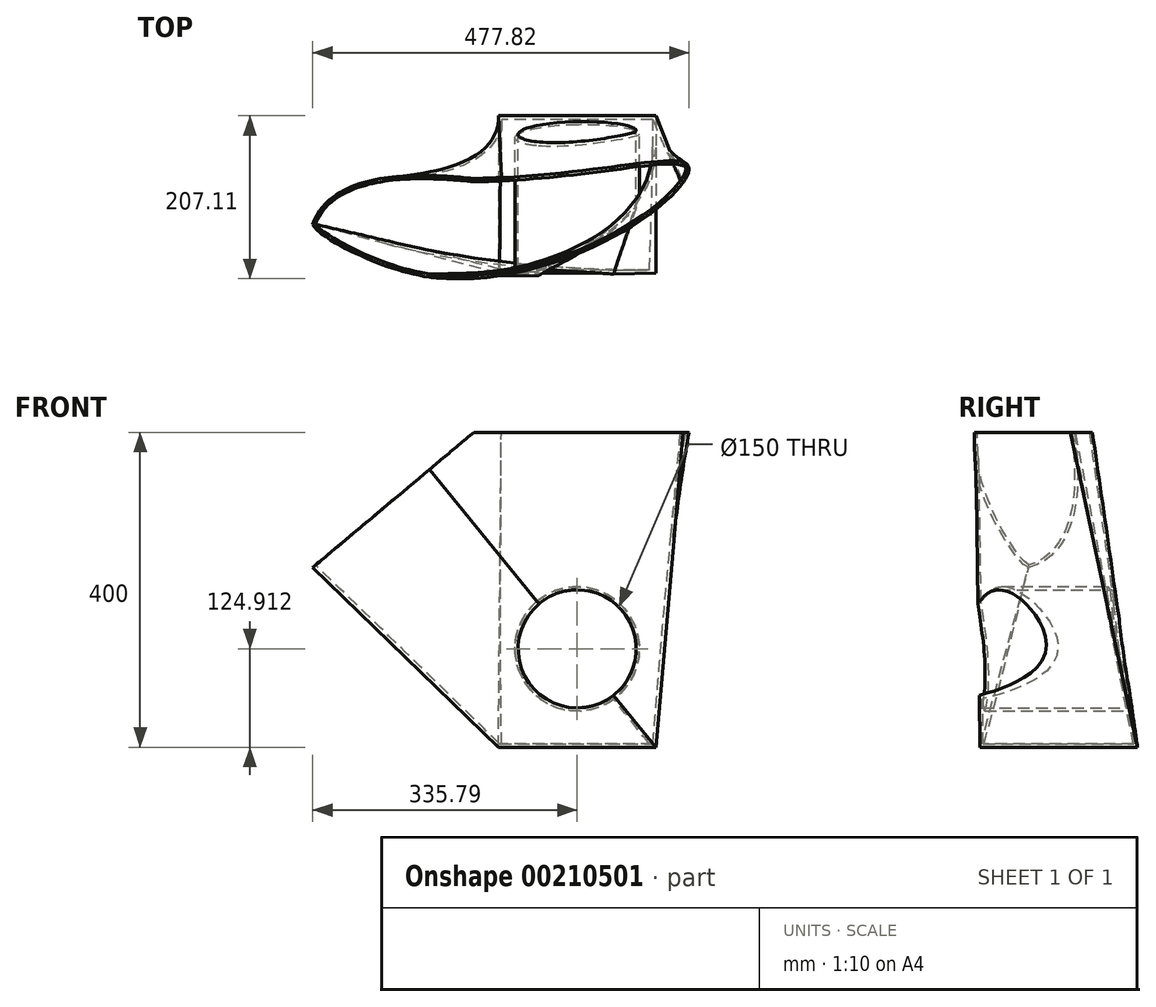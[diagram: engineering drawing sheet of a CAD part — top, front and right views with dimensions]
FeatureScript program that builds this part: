
annotation { "Feature Type Name" : "Feature", "Feature Type Description" : "" }
export const myFeature = defineFeature(function(context is Context, id is Id, definition is map)
    precondition{}
    {
        {
            var Q0;
            Q0=qCreatedBy(makeId("Top.planeOp"),FACE);
            var sketch = newSketch(context, id + "F0", { "sketchPlane" : qUnion([Q0])});
            skLineSegment(sketch, "E0.rect.bottom", {"start": v(-100, 100) * mm, "end": v(100, 100) * mm});
            skLineSegment(sketch, "E0.rect.top", {"start": v(-100, -100) * mm, "end": v(100, -100) * mm});
            skLineSegment(sketch, "E0.rect.left", {"start": v(-100, 100) * mm, "end": v(-100, -100) * mm});
            skLineSegment(sketch, "E0.rect.right", {"start": v(100, 100) * mm, "end": v(100, -100) * mm});
            skPoint(sketch, "E0.rect.middle", {"position": v(0, 0) * mm});
            skSolve(sketch);
        }
        {
            var Q0;
            Q0=qCreatedBy(makeId("Top.planeOp"),FACE);
            cPlane(context, id + "F1", {"entities" : qUnion([Q0]), "cplaneType" : CPlaneType.OFFSET, "offset" : 400 * mm, "width" : 150 * mm, "height" : 150 * mm});
        }
        {
            var Q0;
            Q0=qCreatedBy(id+"F1.planeOp",FACE);
            var sketch = newSketch(context, id + "F2", { "sketchPlane" : qUnion([Q0])});
            skFitSpline(sketch, "E1", {"points": [v(-520.65, 0) * mm, v(-72.7, 22.78) * mm, v(141.98, 33.22) * mm, v(-117.9, -105.72) * mm, v(-520.65, 0) * mm]});
            skSolve(sketch);
        }
        {
            var Q0;
            Q0=makeQuery(id+"F0.imprint","IMPRINT",FACE,{"disambiguationData":[TD([[makeQuery(id+"F0.imprint","IMPRINT",EDGE,{"derivedFrom":sQuery(id+"F0.wireOp",EDGE,"E0.rect.bottom")}),-1.0]])]});
            var Q1;
            Q1=makeQuery(id+"F2.imprint","IMPRINT",FACE,{"disambiguationData":[TD([[makeQuery(id+"F2.imprint","IMPRINT",EDGE,{"derivedFrom":sQuery(id+"F2.wireOp",EDGE,"E1")}),-1.0]])]});
            loft(context, id + "F3", {"sheetProfilesArray" : [{ "sheetProfileEntities" : qUnion([Q0]) }, { "sheetProfileEntities" : qUnion([Q1]) }]});
        }
        {
            var Q0;
            Q0=qCreatedBy(makeId("Front.planeOp"),FACE);
            var sketch = newSketch(context, id + "F4", { "sketchPlane" : qUnion([Q0])});
            skCircle(sketch, "E2", {"center": v(0, 124.91) * mm, "radius": 75 * mm});
            skSolve(sketch);
        }
        {
            var Q0;
            Q0=makeQuery(id+"F4.imprint","IMPRINT",FACE,{"disambiguationData":[TD([[makeQuery(id+"F4.imprint","IMPRINT",EDGE,{"derivedFrom":sQuery(id+"F4.wireOp",EDGE,"E2")}),1.0]])]});
            extrude(context, id + "F5", {"entities" : qUnion([Q0]), "operationType" : NewBodyOperationType.REMOVE, "depth" : 429.9 * mm, "symmetric" : true});
        }
        {
            var Q0;
            Q0=makeQuery(id+"F3.opLoft","CAP_FACE",FACE,{"disambiguationData":[OSD([makeQuery(id+"F2.imprint","IMPRINT",FACE,{"disambiguationData":[TD([[makeQuery(id+"F2.imprint","IMPRINT",EDGE,{"derivedFrom":sQuery(id+"F2.wireOp",EDGE,"E1")}),-1.0]])]})])],"isStart":true});
            shell(context, id + "F6", {"entities" : qUnion([Q0]), "thickness" : 4 * mm});
        }
        {
            var Q0;
            Q0=qCreatedBy(makeId("Top.planeOp"),FACE);
            var sketch = newSketch(context, id + "F7", { "sketchPlane" : qUnion([Q0])});
            skLineSegment(sketch, "E3", {"start": v(500, 0) * mm, "end": v(600, 0) * mm});
            skLineSegment(sketch, "E4", {"start": v(600, 0) * mm, "end": v(550, 86.6) * mm});
            skLineSegment(sketch, "E5", {"start": v(550, 86.6) * mm, "end": v(500, 0) * mm});
            skSolve(sketch);
        }
        {
            var Q0;
            Q0=makeQuery(id+"F7.imprint","IMPRINT",FACE,{"disambiguationData":[TD([[makeQuery(id+"F7.imprint","IMPRINT",EDGE,{"derivedFrom":sQuery(id+"F7.wireOp",EDGE,"E3")}),1.0]])]});
            extrude(context, id + "F8", {"entities" : qUnion([Q0]), "depth" : 200 * mm});
        }
        {
            var Q0;
            Q0=qCreatedBy(makeId("Front.planeOp"),FACE);
            var sketch = newSketch(context, id + "F9", { "sketchPlane" : qUnion([Q0])});
            skLineSegment(sketch, "E6", {"start": v(-451.35, 131.43) * mm, "end": v(-69.83, 451.57) * mm});
            skLineSegment(sketch, "E7", {"start": v(-451.35, 131.43) * mm, "end": v(-703.86, 497.1) * mm});
            skLineSegment(sketch, "E8", {"start": v(-703.86, 497.1) * mm, "end": v(-69.83, 451.57) * mm});
            skSolve(sketch);
        }
        {
            var Q0;
            Q0=makeQuery(id+"F9.imprint","IMPRINT",FACE,{"disambiguationData":[TD([[makeQuery(id+"F9.imprint","IMPRINT",EDGE,{"derivedFrom":sQuery(id+"F9.wireOp",EDGE,"E6")}),1.0]])]});
            extrude(context, id + "F10", {"entities" : qUnion([Q0]), "operationType" : NewBodyOperationType.REMOVE, "oppositeDirection" : true, "depth" : 529.6 * mm, "symmetric" : true});
        }
        {
            var Q0;
            Q0=makeQuery(id+"F8.opExtrude","SWEPT_BODY",BODY,{"disambiguationData":[OSD([sQuery(id+"F7.wireOp",EDGE,"E3"),sQuery(id+"F7.wireOp",EDGE,"E4"),sQuery(id+"F7.wireOp",EDGE,"E5")])]});
            deleteBodies(context, id + "F11", {"entities" : qUnion([Q0])});
        }
    });
